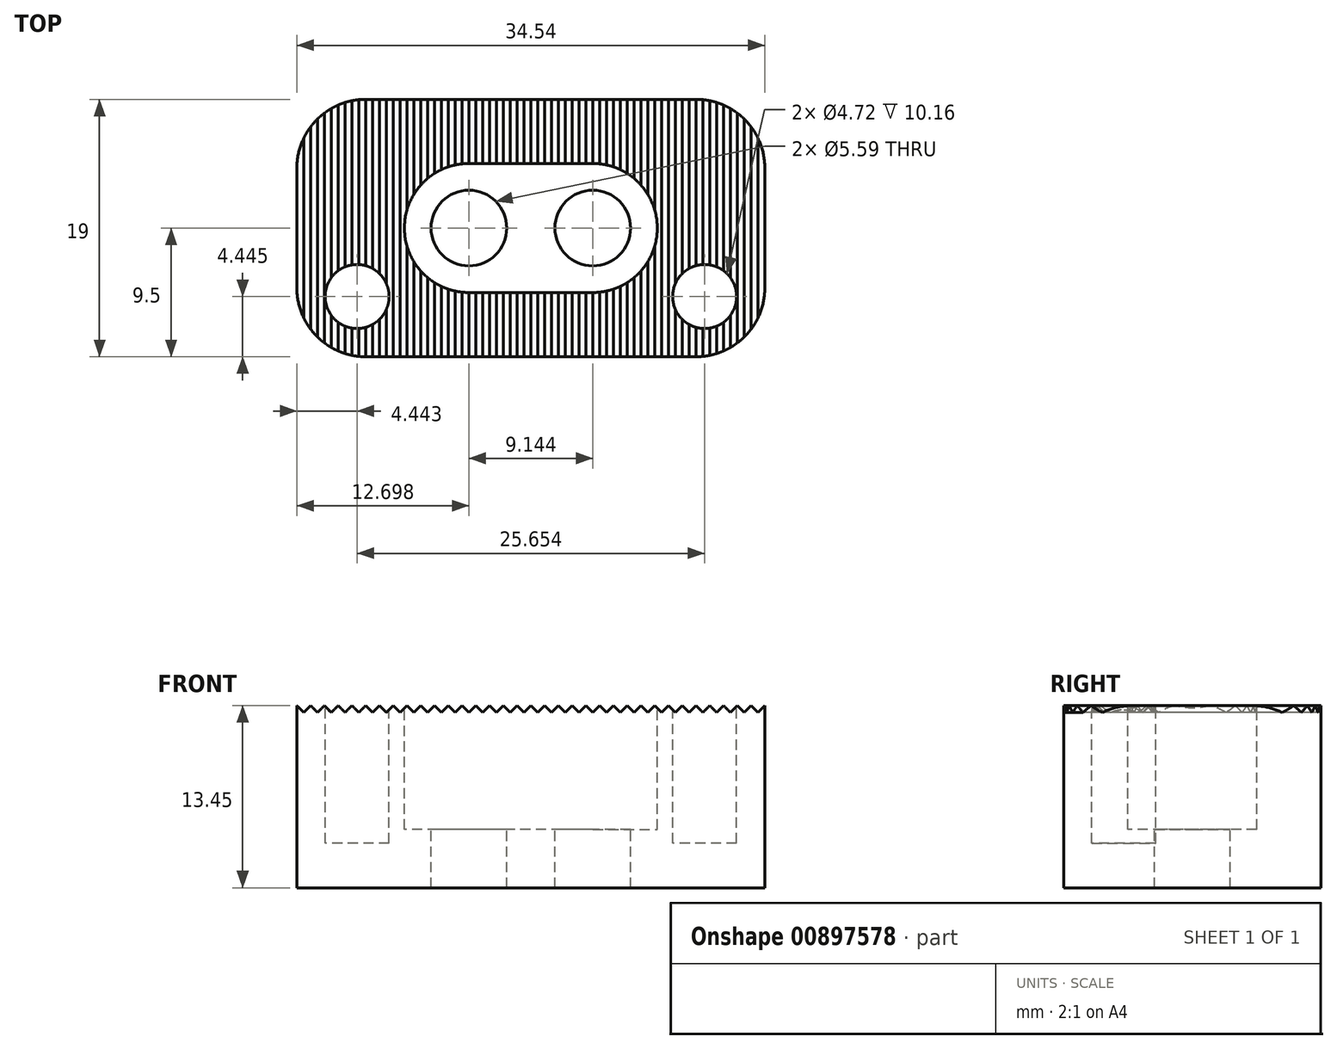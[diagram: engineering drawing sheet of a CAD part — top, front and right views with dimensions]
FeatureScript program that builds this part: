
annotation { "Feature Type Name" : "Feature", "Feature Type Description" : "" }
export const myFeature = defineFeature(function(context is Context, id is Id, definition is map)
    precondition{}
    {
        {
            var Q0;
            Q0=qCreatedBy(makeId("Top.planeOp"),FACE);
            var sketch = newSketch(context, id + "F0", { "sketchPlane" : qUnion([Q0])});
            skLineSegment(sketch, "E0.bottom", {"start": v(17.27, -9.5) * mm, "end": v(-17.27, -9.5) * mm});
            skLineSegment(sketch, "E0.top", {"start": v(17.27, 9.5) * mm, "end": v(-17.27, 9.5) * mm});
            skLineSegment(sketch, "E0.left", {"start": v(17.27, -9.5) * mm, "end": v(17.27, 9.5) * mm});
            skLineSegment(sketch, "E0.right", {"start": v(-17.27, -9.5) * mm, "end": v(-17.27, 9.5) * mm});
            skPoint(sketch, "E0.middle", {"position": v(0, 0) * mm});
            skSolve(sketch);
        }
        {
            var Q0;
            Q0 = qSketchRegion(id + "F0", true);
            extrude(context, id + "F1", {"entities" : qUnion([Q0]), "depth" : 12.7 * mm + .75 * mm, "offsetDistance" : 25.4 * mm});
        }
        {
            var Q0;
            Q0=makeQuery(id+"F1.opExtrude","CAP_FACE",FACE,{"disambiguationData":[OSD([sQuery(id+"F0.wireOp",EDGE,"E0.bottom"),sQuery(id+"F0.wireOp",EDGE,"E0.top"),sQuery(id+"F0.wireOp",EDGE,"E0.left"),sQuery(id+"F0.wireOp",EDGE,"E0.right")])],"isStart":false});
            var sketch = newSketch(context, id + "F2", { "sketchPlane" : qUnion([Q0])});
            skCircle(sketch, "E1", {"center": v(-4.57, 0) * mm, "radius": 4.76 * mm});
            skCircle(sketch, "E2", {"center": v(4.57, 0) * mm, "radius": 4.76 * mm});
            skLineSegment(sketch, "E3", {"start": v(-17.27, 0) * mm, "end": v(17.27, 0) * mm, "construction": true});
            skLineSegment(sketch, "E4", {"start": v(0, 9.5) * mm, "end": v(0, -9.5) * mm, "construction": true});
            skLineSegment(sketch, "E5", {"start": v(-4.57, 4.76) * mm, "end": v(4.57, 4.76) * mm});
            skLineSegment(sketch, "E6", {"start": v(4.57, -4.76) * mm, "end": v(-4.57, -4.76) * mm});
            skLineSegment(sketch, "E7", {"start": v(-4.57, 4.76) * mm, "end": v(-4.57, -4.76) * mm});
            skLineSegment(sketch, "E8", {"start": v(4.57, 4.76) * mm, "end": v(4.57, -4.76) * mm});
            skSolve(sketch);
        }
        {
            var Q0;
            Q0 = qSketchRegion(id + "F2", true);
            var Q1;
            {var subQ0=sQuery(id+"F2.wireOp",EDGE,"E2");var subQ1=sQuery(id+"F2.wireOp",EDGE,"E1");var subQ2=makeQuery(id+"F2.imprint","INTERSECT",VERTEX,{"disambiguationData":[OD(0.0)],"derivedFrom":[subQ1,subQ0]});Q1=makeQuery(id+"F2.imprint","IMPRINT",FACE,{"disambiguationData":[TD([[makeQuery(id+"F2.imprint","IMPRINT",EDGE,{"disambiguationData":[TD([[subQ2,1.0]])],"derivedFrom":subQ1}),1.0]])]});}
            extrude(context, id + "F3", {"entities" : qUnion([Q0, Q1]), "operationType" : NewBodyOperationType.REMOVE, "oppositeDirection" : true, "depth" : 9.14 * mm, "offsetDistance" : 25.4 * mm});
        }
        {
            var Q0;
            Q0=makeQuery(id+"F3.boolean.opBoolean","COPY",FACE,{"derivedFrom":makeQuery(id+"F3.opExtrude","CAP_FACE",FACE,{"disambiguationData":[OSD([sQuery(id+"F2.wireOp",EDGE,"E1"),sQuery(id+"F2.wireOp",EDGE,"E2"),sQuery(id+"F2.wireOp",EDGE,"E5"),sQuery(id+"F2.wireOp",EDGE,"E6")])],"isStart":false})});
            var sketch = newSketch(context, id + "F4", { "sketchPlane" : qUnion([Q0])});
            skCircle(sketch, "E9", {"center": v(-4.57, 0) * mm, "radius": 2.8 * mm});
            skCircle(sketch, "E10", {"center": v(4.57, 0) * mm, "radius": 2.8 * mm});
            skSolve(sketch);
        }
        {
            var Q0;
            Q0 = qSketchRegion(id + "F4", true);
            extrude(context, id + "F5", {"entities" : qUnion([Q0]), "operationType" : NewBodyOperationType.REMOVE, "endBound" : BoundingType.THROUGH_ALL, "oppositeDirection" : true, "depth" : 25.4 * mm, "offsetDistance" : 25.4 * mm});
        }
        {
            var Q0;
            Q0=makeQuery(id+"F1.opExtrude","CAP_FACE",FACE,{"disambiguationData":[OSD([sQuery(id+"F0.wireOp",EDGE,"E0.bottom"),sQuery(id+"F0.wireOp",EDGE,"E0.top"),sQuery(id+"F0.wireOp",EDGE,"E0.left"),sQuery(id+"F0.wireOp",EDGE,"E0.right")])],"isStart":false});
            var sketch = newSketch(context, id + "F6", { "sketchPlane" : qUnion([Q0])});
            skCircle(sketch, "E11", {"center": v(-12.83, -5.06) * mm, "radius": 2.36 * mm});
            skCircle(sketch, "E12", {"center": v(12.83, -5.06) * mm, "radius": 2.36 * mm});
            skSolve(sketch);
        }
        {
            var Q0;
            Q0 = qSketchRegion(id + "F6", true);
            extrude(context, id + "F7", {"entities" : qUnion([Q0]), "operationType" : NewBodyOperationType.REMOVE, "oppositeDirection" : true, "depth" : 10.16 * mm, "offsetDistance" : 25.4 * mm});
        }
        {
            var Q0;
            Q0=makeQuery(id+"F1.opExtrude","SWEPT_FACE",FACE,{"disambiguationData":[OSD([sQuery(id+"F0.wireOp",EDGE,"E0.bottom")])]});
            var sketch = newSketch(context, id + "F8", { "sketchPlane" : qUnion([Q0])});
            skLineSegment(sketch, "E13", {"start": v(17.27, 13.45) * mm, "end": v(16.76, 12.94) * mm});
            skLineSegment(sketch, "E14", {"start": v(16.76, 12.94) * mm, "end": v(16.26, 13.45) * mm});
            skLineSegment(sketch, "E15.1.0.0", {"start": v(16.26, 13.45) * mm, "end": v(15.75, 12.94) * mm});
            skLineSegment(sketch, "E15.1.0.1", {"start": v(15.75, 12.94) * mm, "end": v(15.24, 13.45) * mm});
            skLineSegment(sketch, "E15.2.0.0", {"start": v(15.24, 13.45) * mm, "end": v(14.73, 12.94) * mm});
            skLineSegment(sketch, "E15.2.0.1", {"start": v(14.73, 12.94) * mm, "end": v(14.22, 13.45) * mm});
            skLineSegment(sketch, "E15.3.0.0", {"start": v(14.22, 13.45) * mm, "end": v(13.72, 12.94) * mm});
            skLineSegment(sketch, "E15.3.0.1", {"start": v(13.72, 12.94) * mm, "end": v(13.2, 13.45) * mm});
            skLineSegment(sketch, "E15.4.0.0", {"start": v(13.2, 13.45) * mm, "end": v(12.7, 12.94) * mm});
            skLineSegment(sketch, "E15.4.0.1", {"start": v(12.7, 12.94) * mm, "end": v(12.2, 13.45) * mm});
            skLineSegment(sketch, "E15.5.0.0", {"start": v(12.2, 13.45) * mm, "end": v(11.68, 12.94) * mm});
            skLineSegment(sketch, "E15.5.0.1", {"start": v(11.68, 12.94) * mm, "end": v(11.18, 13.45) * mm});
            skLineSegment(sketch, "E15.6.0.0", {"start": v(11.18, 13.45) * mm, "end": v(10.67, 12.94) * mm});
            skLineSegment(sketch, "E15.6.0.1", {"start": v(10.67, 12.94) * mm, "end": v(10.16, 13.45) * mm});
            skLineSegment(sketch, "E15.7.0.0", {"start": v(10.16, 13.45) * mm, "end": v(9.65, 12.94) * mm});
            skLineSegment(sketch, "E15.7.0.1", {"start": v(9.65, 12.94) * mm, "end": v(9.14, 13.45) * mm});
            skLineSegment(sketch, "E15.8.0.0", {"start": v(9.14, 13.45) * mm, "end": v(8.64, 12.94) * mm});
            skLineSegment(sketch, "E15.8.0.1", {"start": v(8.64, 12.94) * mm, "end": v(8.13, 13.45) * mm});
            skLineSegment(sketch, "E15.9.0.0", {"start": v(8.13, 13.45) * mm, "end": v(7.62, 12.94) * mm});
            skLineSegment(sketch, "E15.9.0.1", {"start": v(7.62, 12.94) * mm, "end": v(7.11, 13.45) * mm});
            skLineSegment(sketch, "E15.10.0.0", {"start": v(7.11, 13.45) * mm, "end": v(6.6, 12.94) * mm});
            skLineSegment(sketch, "E15.10.0.1", {"start": v(6.6, 12.94) * mm, "end": v(6.1, 13.45) * mm});
            skLineSegment(sketch, "E15.11.0.0", {"start": v(6.1, 13.45) * mm, "end": v(5.59, 12.94) * mm});
            skLineSegment(sketch, "E15.11.0.1", {"start": v(5.59, 12.94) * mm, "end": v(5.08, 13.45) * mm});
            skLineSegment(sketch, "E15.12.0.0", {"start": v(5.08, 13.45) * mm, "end": v(4.57, 12.94) * mm});
            skLineSegment(sketch, "E15.12.0.1", {"start": v(4.57, 12.94) * mm, "end": v(4.06, 13.45) * mm});
            skLineSegment(sketch, "E15.13.0.0", {"start": v(4.06, 13.45) * mm, "end": v(3.56, 12.94) * mm});
            skLineSegment(sketch, "E15.13.0.1", {"start": v(3.56, 12.94) * mm, "end": v(3.05, 13.45) * mm});
            skLineSegment(sketch, "E15.14.0.0", {"start": v(3.05, 13.45) * mm, "end": v(2.54, 12.94) * mm});
            skLineSegment(sketch, "E15.14.0.1", {"start": v(2.54, 12.94) * mm, "end": v(2.03, 13.45) * mm});
            skLineSegment(sketch, "E15.15.0.0", {"start": v(2.03, 13.45) * mm, "end": v(1.52, 12.94) * mm});
            skLineSegment(sketch, "E15.15.0.1", {"start": v(1.52, 12.94) * mm, "end": v(1.02, 13.45) * mm});
            skLineSegment(sketch, "E15.16.0.0", {"start": v(1.02, 13.45) * mm, "end": v(0.5, 12.94) * mm});
            skLineSegment(sketch, "E15.16.0.1", {"start": v(0.5, 12.94) * mm, "end": v(0, 13.45) * mm});
            skLineSegment(sketch, "E15.17.0.0", {"start": v(0, 13.45) * mm, "end": v(-0.5, 12.94) * mm});
            skLineSegment(sketch, "E15.17.0.1", {"start": v(-0.5, 12.94) * mm, "end": v(-1.02, 13.45) * mm});
            skLineSegment(sketch, "E15.18.0.0", {"start": v(-1.02, 13.45) * mm, "end": v(-1.52, 12.94) * mm});
            skLineSegment(sketch, "E15.18.0.1", {"start": v(-1.52, 12.94) * mm, "end": v(-2.03, 13.45) * mm});
            skLineSegment(sketch, "E15.19.0.0", {"start": v(-2.03, 13.45) * mm, "end": v(-2.54, 12.94) * mm});
            skLineSegment(sketch, "E15.19.0.1", {"start": v(-2.54, 12.94) * mm, "end": v(-3.05, 13.45) * mm});
            skLineSegment(sketch, "E15.direction1", {"start": v(16.76, 12.94) * mm, "end": v(15.75, 12.94) * mm, "construction": true});
            skLineSegment(sketch, "E16.0.20.0", {"start": v(-3.05, 13.45) * mm, "end": v(-3.56, 12.94) * mm});
            skLineSegment(sketch, "E16.3.20.0", {"start": v(-3.56, 12.94) * mm, "end": v(-4.06, 13.45) * mm});
            skLineSegment(sketch, "E16.0.21.0", {"start": v(-4.06, 13.45) * mm, "end": v(-4.57, 12.94) * mm});
            skLineSegment(sketch, "E16.3.21.0", {"start": v(-4.57, 12.94) * mm, "end": v(-5.08, 13.45) * mm});
            skLineSegment(sketch, "E16.0.22.0", {"start": v(-5.08, 13.45) * mm, "end": v(-5.59, 12.94) * mm});
            skLineSegment(sketch, "E16.3.22.0", {"start": v(-5.59, 12.94) * mm, "end": v(-6.1, 13.45) * mm});
            skLineSegment(sketch, "E16.0.23.0", {"start": v(-6.1, 13.45) * mm, "end": v(-6.6, 12.94) * mm});
            skLineSegment(sketch, "E16.3.23.0", {"start": v(-6.6, 12.94) * mm, "end": v(-7.11, 13.45) * mm});
            skLineSegment(sketch, "E16.0.24.0", {"start": v(-7.11, 13.45) * mm, "end": v(-7.62, 12.94) * mm});
            skLineSegment(sketch, "E16.3.24.0", {"start": v(-7.62, 12.94) * mm, "end": v(-8.13, 13.45) * mm});
            skLineSegment(sketch, "E16.0.25.0", {"start": v(-8.13, 13.45) * mm, "end": v(-8.64, 12.94) * mm});
            skLineSegment(sketch, "E16.3.25.0", {"start": v(-8.64, 12.94) * mm, "end": v(-9.14, 13.45) * mm});
            skLineSegment(sketch, "E16.0.26.0", {"start": v(-9.14, 13.45) * mm, "end": v(-9.65, 12.94) * mm});
            skLineSegment(sketch, "E16.3.26.0", {"start": v(-9.65, 12.94) * mm, "end": v(-10.16, 13.45) * mm});
            skLineSegment(sketch, "E16.0.27.0", {"start": v(-10.16, 13.45) * mm, "end": v(-10.67, 12.94) * mm});
            skLineSegment(sketch, "E16.3.27.0", {"start": v(-10.67, 12.94) * mm, "end": v(-11.18, 13.45) * mm});
            skLineSegment(sketch, "E16.0.28.0", {"start": v(-11.18, 13.45) * mm, "end": v(-11.68, 12.94) * mm});
            skLineSegment(sketch, "E16.3.28.0", {"start": v(-11.68, 12.94) * mm, "end": v(-12.2, 13.45) * mm});
            skLineSegment(sketch, "E16.0.29.0", {"start": v(-12.2, 13.45) * mm, "end": v(-12.7, 12.94) * mm});
            skLineSegment(sketch, "E16.3.29.0", {"start": v(-12.7, 12.94) * mm, "end": v(-13.2, 13.45) * mm});
            skLineSegment(sketch, "E16.0.30.0", {"start": v(-13.2, 13.45) * mm, "end": v(-13.72, 12.94) * mm});
            skLineSegment(sketch, "E16.3.30.0", {"start": v(-13.72, 12.94) * mm, "end": v(-14.22, 13.45) * mm});
            skLineSegment(sketch, "E17", {"start": v(17.27, 13.45) * mm, "end": v(-14.22, 13.45) * mm});
            skLineSegment(sketch, "E18.0.31.0", {"start": v(-14.22, 13.45) * mm, "end": v(-14.73, 12.94) * mm});
            skLineSegment(sketch, "E18.3.31.0", {"start": v(-14.73, 12.94) * mm, "end": v(-15.24, 13.45) * mm});
            skLineSegment(sketch, "E18.0.32.0", {"start": v(-15.24, 13.45) * mm, "end": v(-15.75, 12.94) * mm});
            skLineSegment(sketch, "E18.3.32.0", {"start": v(-15.75, 12.94) * mm, "end": v(-16.26, 13.45) * mm});
            skLineSegment(sketch, "E18.0.33.0", {"start": v(-16.26, 13.45) * mm, "end": v(-16.76, 12.94) * mm});
            skLineSegment(sketch, "E18.3.33.0", {"start": v(-16.76, 12.94) * mm, "end": v(-17.27, 13.45) * mm});
            skLineSegment(sketch, "E18.0.34.0", {"start": v(-17.27, 13.45) * mm, "end": v(-17.78, 12.94) * mm});
            skLineSegment(sketch, "E18.3.34.0", {"start": v(-17.78, 12.94) * mm, "end": v(-18.29, 13.45) * mm});
            skLineSegment(sketch, "E19", {"start": v(-18.29, 13.45) * mm, "end": v(-10.16, 13.45) * mm});
            skSolve(sketch);
        }
        {
            var Q0;
            Q0 = qSketchRegion(id + "F8", true);
            extrude(context, id + "F9", {"entities" : qUnion([Q0]), "operationType" : NewBodyOperationType.REMOVE, "endBound" : BoundingType.THROUGH_ALL, "oppositeDirection" : true, "depth" : 25.4 * mm, "offsetDistance" : 25.4 * mm});
        }
        {
            var Q0;
            Q0=makeQuery(id+"F1.opExtrude","SWEPT_EDGE",EDGE,{"disambiguationData":[OSD([sQuery(id+"F0.wireOp",EDGE,"E0.bottom"),sQuery(id+"F0.wireOp",EDGE,"E0.right")])]});
            var Q1;
            Q1=makeQuery(id+"F1.opExtrude","SWEPT_EDGE",EDGE,{"disambiguationData":[OSD([sQuery(id+"F0.wireOp",EDGE,"E0.bottom"),sQuery(id+"F0.wireOp",EDGE,"E0.left")])]});
            var Q2;
            Q2=makeQuery(id+"F1.opExtrude","SWEPT_EDGE",EDGE,{"disambiguationData":[OSD([sQuery(id+"F0.wireOp",EDGE,"E0.top"),sQuery(id+"F0.wireOp",EDGE,"E0.left")])]});
            var Q3;
            Q3=makeQuery(id+"F1.opExtrude","SWEPT_EDGE",EDGE,{"disambiguationData":[OSD([sQuery(id+"F0.wireOp",EDGE,"E0.top"),sQuery(id+"F0.wireOp",EDGE,"E0.right")])]});
            fillet(context, id + "F10", {"entities" : qUnion([Q0, Q1, Q2, Q3]), "radius" : 5.08 * mm, "tangentPropagation" : true, "allowEdgeOverflow" : false});
        }
    });
